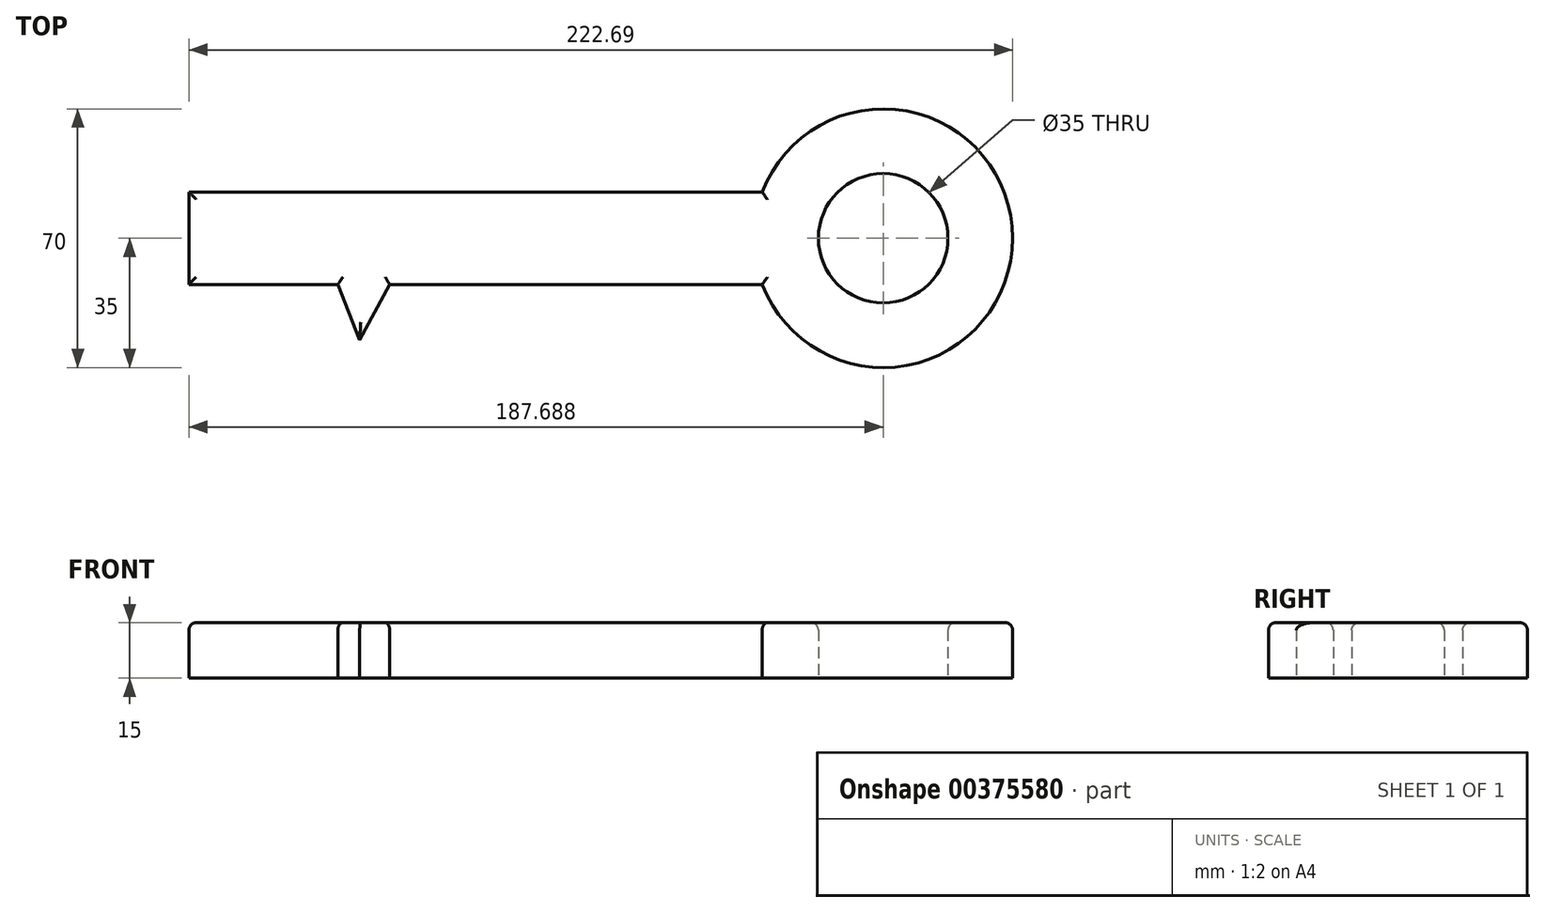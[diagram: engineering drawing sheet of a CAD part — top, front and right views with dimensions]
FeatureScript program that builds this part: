
annotation { "Feature Type Name" : "Feature", "Feature Type Description" : "" }
export const myFeature = defineFeature(function(context is Context, id is Id, definition is map)
    precondition{}
    {
        {
            var Q0;
            Q0=qCreatedBy(makeId("Top.planeOp"),FACE);
            var sketch = newSketch(context, id + "F0", { "sketchPlane" : qUnion([Q0])});
            skLineSegment(sketch, "E0.bottom", {"start": v(-72.98, 25) * mm, "end": v(82.02, 25) * mm});
            skLineSegment(sketch, "E0.top", {"start": v(-72.98, 0) * mm, "end": v(82.02, 0) * mm});
            skLineSegment(sketch, "E0.left", {"start": v(-72.98, 25) * mm, "end": v(-72.98, 0) * mm});
            skLineSegment(sketch, "E0.right", {"start": v(82.02, 25) * mm, "end": v(82.02, 0) * mm});
            skLineSegment(sketch, "E1.bottom", {"start": v(-72.98, 0) * mm, "end": v(-62.98, 0) * mm});
            skLineSegment(sketch, "E1.top", {"start": v(-72.98, -30) * mm, "end": v(-62.98, -30) * mm});
            skLineSegment(sketch, "E1.left", {"start": v(-72.98, 0) * mm, "end": v(-72.98, -30) * mm});
            skLineSegment(sketch, "E1.right", {"start": v(-62.98, 0) * mm, "end": v(-62.98, -30) * mm});
            skLineSegment(sketch, "E2.bottom", {"start": v(-51.63, 0) * mm, "end": v(-43.63, 0) * mm});
            skLineSegment(sketch, "E2.top", {"start": v(-51.63, -15) * mm, "end": v(-43.63, -15) * mm});
            skLineSegment(sketch, "E2.left", {"start": v(-51.63, 0) * mm, "end": v(-51.63, -15) * mm});
            skLineSegment(sketch, "E2.right", {"start": v(-43.63, 0) * mm, "end": v(-43.63, -15) * mm});
            skLineSegment(sketch, "E3", {"start": v(-32.7, 0) * mm, "end": v(-26.79, -15) * mm});
            skLineSegment(sketch, "E4", {"start": v(-26.79, -15) * mm, "end": v(-18.7, 0) * mm});
            skArc(sketch, "E5", {"start": v(82.02, 0) * mm, "mid": v(149.7, 12.5) * mm, "end": v(82.02, 25) * mm});
            skCircle(sketch, "E6", {"center": v(114.7, 12.5) * mm, "radius": 17.5 * mm});
            skSolve(sketch);
        }
        {
            var Q0;
            Q0=makeQuery(id+"F0.imprint","IMPRINT",FACE,{"disambiguationData":[TD([[makeQuery(id+"F0.imprint","IMPRINT",EDGE,{"derivedFrom":sQuery(id+"F0.wireOp",EDGE,"E0.bottom")}),-1.0]])]});
            var Q1;
            Q1=makeQuery(id+"F0.imprint","IMPRINT",FACE,{"disambiguationData":[TD([[makeQuery(id+"F0.imprint","IMPRINT",EDGE,{"derivedFrom":sQuery(id+"F0.wireOp",EDGE,"E1.bottom")}),-1.0]])]});
            var Q2;
            Q2=makeQuery(id+"F0.imprint","IMPRINT",FACE,{"disambiguationData":[TD([[makeQuery(id+"F0.imprint","IMPRINT",EDGE,{"derivedFrom":sQuery(id+"F0.wireOp",EDGE,"E2.bottom")}),-1.0]])]});
            var Q3;
            {var subQ0=sQuery(id+"F0.wireOp",EDGE,"E3");Q3=makeQuery(id+"F0.imprint","IMPRINT",FACE,{"disambiguationData":[TD([[makeQuery(id+"F0.imprint","IMPRINT",EDGE,{"derivedFrom":subQ0}),1.0]])]});}
            var Q4;
            Q4=makeQuery(id+"F0.imprint","IMPRINT",FACE,{"disambiguationData":[TD([[makeQuery(id+"F0.imprint","IMPRINT",EDGE,{"derivedFrom":sQuery(id+"F0.wireOp",EDGE,"E0.right")}),1.0]])]});
            extrude(context, id + "F1", {"entities" : qUnion([Q0, Q1, Q2, Q3, Q4]), "depth" : 15 * mm});
        }
        {
            var Q0;
            Q0=makeQuery(id+"F1.opExtrude","CAP_EDGE",EDGE,{"disambiguationData":[OSD([sQuery(id+"F0.wireOp",EDGE,"E0.left"),sQuery(id+"F0.wireOp",EDGE,"E1.left")])],"isStart":false});
            var Q1;
            Q1=makeQuery(id+"F1.opExtrude","CAP_EDGE",EDGE,{"disambiguationData":[OSD([sQuery(id+"F0.wireOp",EDGE,"E1.right")])],"isStart":false});
            var Q2;
            Q2=makeQuery(id+"F1.opExtrude","CAP_EDGE",EDGE,{"disambiguationData":[OSD([sQuery(id+"F0.wireOp",EDGE,"E1.top")])],"isStart":false});
            var Q3;
            Q3=makeQuery(id+"F1.opExtrude","CAP_EDGE",EDGE,{"disambiguationData":[OSD([sQuery(id+"F0.wireOp",EDGE,"E2.top")])],"isStart":false});
            var Q4;
            Q4=makeQuery(id+"F1.opExtrude","CAP_EDGE",EDGE,{"disambiguationData":[OSD([sQuery(id+"F0.wireOp",EDGE,"E2.right")])],"isStart":false});
            var Q5;
            Q5=makeQuery(id+"F1.opExtrude","CAP_EDGE",EDGE,{"disambiguationData":[OSD([sQuery(id+"F0.wireOp",EDGE,"E3")])],"isStart":false});
            var Q6;
            Q6=makeQuery(id+"F1.opExtrude","CAP_EDGE",EDGE,{"disambiguationData":[OSD([sQuery(id+"F0.wireOp",EDGE,"E0.bottom")])],"isStart":false});
            var Q7;
            Q7=makeQuery(id+"F1.opExtrude","CAP_FACE",FACE,{"disambiguationData":[OSD([sQuery(id+"F0.wireOp",EDGE,"E0.bottom"),sQuery(id+"F0.wireOp",EDGE,"E0.top"),sQuery(id+"F0.wireOp",EDGE,"E0.left"),sQuery(id+"F0.wireOp",EDGE,"E1.top"),sQuery(id+"F0.wireOp",EDGE,"E1.left"),sQuery(id+"F0.wireOp",EDGE,"E1.right"),sQuery(id+"F0.wireOp",EDGE,"E2.top"),sQuery(id+"F0.wireOp",EDGE,"E2.left"),sQuery(id+"F0.wireOp",EDGE,"E2.right"),sQuery(id+"F0.wireOp",EDGE,"E3"),sQuery(id+"F0.wireOp",EDGE,"E4"),sQuery(id+"F0.wireOp",EDGE,"E5"),sQuery(id+"F0.wireOp",EDGE,"E6")])],"isStart":false});
            fillet(context, id + "F2", {"entities" : qUnion([Q0, Q1, Q2, Q3, Q4, Q5, Q6, Q7]), "radius" : 2 * mm, "tangentPropagation" : true, "allowEdgeOverflow" : false});
        }
    });
